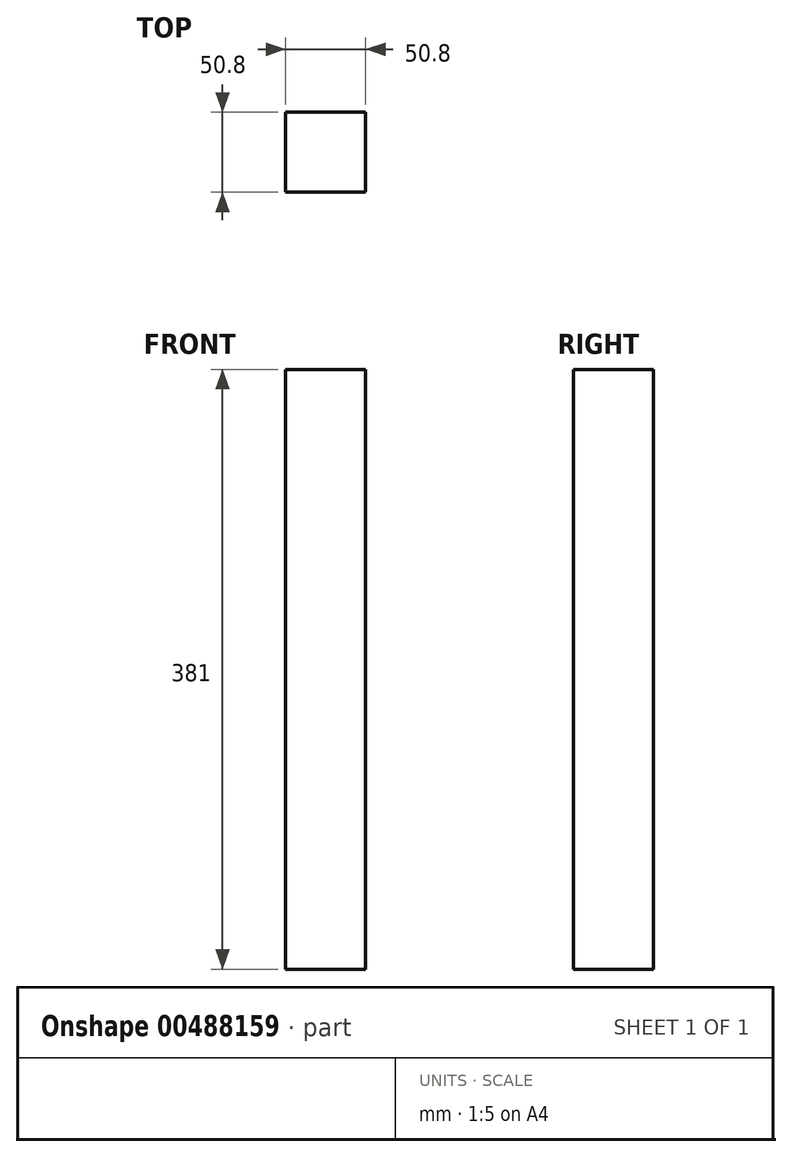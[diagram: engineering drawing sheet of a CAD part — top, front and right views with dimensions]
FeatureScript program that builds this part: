
annotation { "Feature Type Name" : "Feature", "Feature Type Description" : "" }
export const myFeature = defineFeature(function(context is Context, id is Id, definition is map)
    precondition{}
    {
        {
            var Q0;
            Q0=qCreatedBy(makeId("Front.planeOp"),FACE);
            var sketch = newSketch(context, id + "F0", { "sketchPlane" : qUnion([Q0])});
            skLineSegment(sketch, "E0", {"start": v(0, 381) * mm, "end": v(50.8, 381) * mm});
            skLineSegment(sketch, "E1", {"start": v(50.8, 381) * mm, "end": v(50.8, 0) * mm});
            skLineSegment(sketch, "E2", {"start": v(50.8, 0) * mm, "end": v(0, 0) * mm});
            skLineSegment(sketch, "E3", {"start": v(0, 381) * mm, "end": v(0, 0) * mm});
            skSolve(sketch);
        }
        {
            var Q0;
            Q0=makeQuery(id+"F0.imprint","IMPRINT",FACE,{"disambiguationData":[TD([[makeQuery(id+"F0.imprint","IMPRINT",EDGE,{"derivedFrom":sQuery(id+"F0.wireOp",EDGE,"E0")}),-1.0]])]});
            extrude(context, id + "F1", {"entities" : qUnion([Q0]), "depth" : 50.8 * mm, "offsetDistance" : 25.4 * mm});
        }
    });
